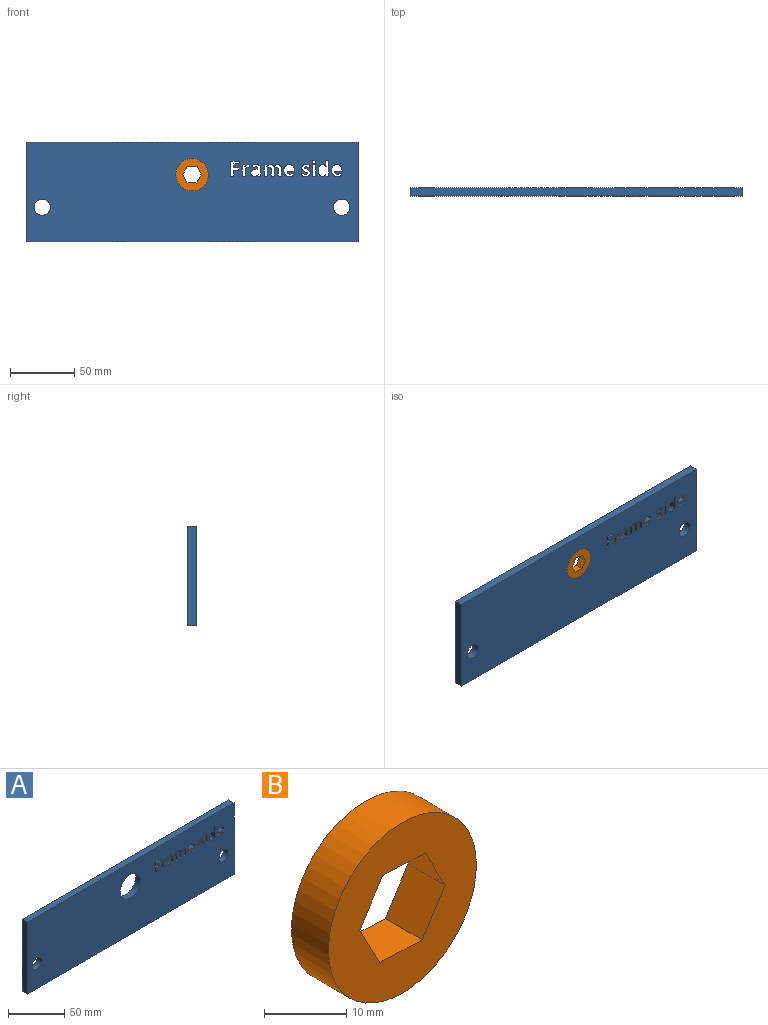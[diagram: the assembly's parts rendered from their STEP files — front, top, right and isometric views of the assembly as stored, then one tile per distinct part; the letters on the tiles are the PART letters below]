
ASSEMBLY  parts=2 mates=1
PART A: 157 faces, bbox 259.1x6.4x77.8 mm
  f0: extruded ~6.35x1.36mm, area 9.2mm2, adj f1,f154,f155,f156
  f1: extruded ~6.35x1.76mm, area 11.3mm2, adj f0,f2,f155,f156
  f2: extruded ~6.35x3.35mm, area 23.2mm2, adj f1,f3,f155,f156
  f3: extruded ~6.35x3.35mm, area 23.3mm2, adj f2,f4,f155,f156
  f4: extruded ~6.35x3.45mm, area 23.6mm2, adj f3,f5,f155,f156
  f5: extruded ~6.35x3.09mm, area 21.7mm2, adj f4,f6,f155,f156
  f6: extruded ~6.35x2.93mm, area 20.4mm2, adj f5,f7,f155,f156
  f7: extruded ~6.35x2.96mm, area 20.5mm2, adj f6,f8,f155,f156
  f8: plane 6.35x1.18mm, normal (-1,0,0), area 7.5mm2, adj f7,f9,f155,f156
  f9: plane 6.35x5.73mm, normal (0,0,1), area 36.4mm2, adj f8,f10,f155,f156
  f10: extruded ~6.35x1.61mm, area 11.2mm2, adj f9,f11,f155,f156
  f11: extruded ~6.35x1.6mm, area 11.1mm2, adj f10,f12,f155,f156
  f12: extruded ~6.35x1.52mm, area 9.7mm2, adj f11,f13,f155,f156
  f13: extruded ~6.35x1.49mm, area 10.1mm2, adj f12,f154,f155,f156
  f14: extruded ~6.35x2.02mm, area 13.3mm2, adj f15,f141,f155,f156
  f15: plane 6.35x4.46mm, normal (-1,0,0), area 28.3mm2, adj f14,f16,f155,f156
  f16: plane 6.35x2.42mm, normal (0,0,1), area 15.4mm2, adj f15,f17,f155,f156
  f17: plane 6.35x5.19mm, normal (1,0,0), area 32.9mm2, adj f16,f18,f155,f156
  f18: extruded ~6.35x1.44mm, area 9.5mm2, adj f17,f19,f155,f156
  f19: extruded ~6.35x1.01mm, area 7.4mm2, adj f18,f20,f155,f156
  f20: extruded ~6.35x1.35mm, area 10.1mm2, adj f19,f21,f155,f156
  f21: extruded ~6.35x2.25mm, area 14.7mm2, adj f20,f22,f155,f156
  f22: plane 6.35x4.18mm, normal (-1,0,0), area 26.5mm2, adj f21,f23,f155,f156
  f23: plane 6.35x2.42mm, normal (0,0,1), area 15.4mm2, adj f22,f24,f155,f156
  f24: plane 8.88x6.35mm, normal (1,0,0), area 56.4mm2, adj f23,f25,f155,f156
  f25: plane 6.35x1.85mm, normal (0,0,-1), area 11.7mm2, adj f24,f26,f155,f156
  f26: plane 6.35x1.14mm, normal (-0.96,0,-0.28), area 7.5mm2, adj f25,f27,f155,f156
  f27: plane 6.35x0.13mm, normal (0,0,-1), area 0.9mm2, adj f26,f28,f155,f156
  f28: extruded ~6.35x1.03mm, area 9.1mm2, adj f27,f29,f155,f156
  f29: extruded ~6.35x1.55mm, area 10.2mm2, adj f28,f30,f155,f156
  f30: extruded ~6.35x2.7mm, area 20.1mm2, adj f29,f31,f155,f156
  f31: plane 6.35x0.21mm, normal (0,0,-1), area 1.4mm2, adj f30,f32,f155,f156
  f32: extruded ~6.35x1.05mm, area 9.2mm2, adj f31,f33,f155,f156
  f33: extruded ~6.35x1.57mm, area 10.3mm2, adj f32,f34,f155,f156
  f34: extruded ~6.35x2.28mm, area 15.7mm2, adj f33,f35,f155,f156
  f35: extruded ~6.35x2.48mm, area 16.9mm2, adj f34,f36,f155,f156
  f36: plane 6.35x5.79mm, normal (-1,0,0), area 36.8mm2, adj f35,f37,f155,f156
  f37: plane 6.35x2.43mm, normal (0,0,1), area 15.4mm2, adj f36,f38,f155,f156
  f38: plane 6.35x5.19mm, normal (1,0,0), area 32.9mm2, adj f37,f39,f155,f156
  f39: extruded ~6.35x1.44mm, area 9.5mm2, adj f38,f40,f155,f156
  f40: extruded ~6.35x1.01mm, area 7.4mm2, adj f39,f141,f155,f156
  f41: plane 6.35x5.92mm, normal (-1,0,0), area 37.6mm2, adj f42,f142,f155,f156
  f42: plane 6.35x1.69mm, normal (0,0,1), area 10.7mm2, adj f41,f43,f155,f156
  f43: plane 6.35x1.21mm, normal (0.93,0,0.36), area 8.2mm2, adj f42,f44,f155,f156
  f44: plane 6.35x0.06mm, normal (0,0,1), area 0.4mm2, adj f43,f45,f155,f156
  f45: extruded ~6.35x1.26mm, area 10.6mm2, adj f44,f46,f155,f156
  f46: extruded ~6.35x1.69mm, area 11mm2, adj f45,f47,f155,f156
  f47: extruded ~6.35x2.01mm, area 14mm2, adj f46,f48,f155,f156
  f48: extruded ~6.35x2.08mm, area 14.4mm2, adj f47,f49,f155,f156
  f49: extruded ~6.35x2.08mm, area 15.3mm2, adj f48,f50,f155,f156
  f50: extruded ~6.35x2.98mm, area 19.8mm2, adj f49,f51,f155,f156
  f51: plane 6.35x1.54mm, normal (0.03,0,-1), area 9.8mm2, adj f50,f52,f155,f156
  f52: plane 6.35x0.39mm, normal (1,0,0), area 2.5mm2, adj f51,f53,f155,f156
  f53: extruded ~6.35x1.38mm, area 14.1mm2, adj f52,f54,f155,f156
  f54: extruded ~6.35x2.5mm, area 16.5mm2, adj f53,f55,f155,f156
  f55: plane 6.35x1.64mm, normal (0.9,0,0.44), area 11.6mm2, adj f54,f56,f155,f156
  f56: extruded ~6.35x3.4mm, area 22.4mm2, adj f55,f57,f155,f156
  f57: extruded ~6.35x2.74mm, area 18.4mm2, adj f56,f142,f155,f156
  f58: extruded ~6.35x1.2mm, area 10.5mm2, adj f59,f143,f155,f156
  f59: extruded ~6.35x1.53mm, area 10.3mm2, adj f58,f60,f155,f156
  f60: extruded ~6.35x0.82mm, area 5.2mm2, adj f59,f61,f155,f156
  f61: plane 6.35x2.27mm, normal (-1,0,0.08), area 14.5mm2, adj f60,f62,f155,f156
  f62: extruded ~6.35x0.71mm, area 4.6mm2, adj f61,f63,f155,f156
  f63: extruded ~6.35x1.81mm, area 12.4mm2, adj f62,f64,f155,f156
  f64: extruded ~6.35x1.67mm, area 11.7mm2, adj f63,f65,f155,f156
  f65: plane 6.35x4.52mm, normal (-1,0,0), area 28.7mm2, adj f64,f66,f155,f156
  f66: plane 6.35x2.42mm, normal (0,0,1), area 15.4mm2, adj f65,f67,f155,f156
  f67: plane 8.88x6.35mm, normal (1,0,0), area 56.4mm2, adj f66,f68,f155,f156
  f68: plane 6.35x1.84mm, normal (0,0,-1), area 11.7mm2, adj f67,f69,f155,f156
  f69: plane 6.35x1.49mm, normal (-0.97,0,-0.23), area 9.8mm2, adj f68,f143,f155,f156
  f70: plane 6.35x3.94mm, normal (0,0,1), area 25mm2, adj f71,f144,f155,f156
  f71: plane 6.35x4.59mm, normal (-1,0,0), area 29.1mm2, adj f70,f72,f155,f156
  f72: plane 6.35x2.42mm, normal (0,0,1), area 15.4mm2, adj f71,f73,f155,f156
  f73: plane 11.61x6.35mm, normal (1,0,0), area 73.7mm2, adj f72,f74,f155,f156
  f74: plane 6.66x6.35mm, normal (0,0,-1), area 42.3mm2, adj f73,f75,f155,f156
  f75: plane 6.35x2.02mm, normal (-1,0,0), area 12.8mm2, adj f74,f76,f155,f156
  f76: plane 6.35x4.23mm, normal (0,0,1), area 26.9mm2, adj f75,f77,f155,f156
  f77: plane 6.35x2.99mm, normal (-1,0,0), area 19mm2, adj f76,f78,f155,f156
  f78: plane 6.35x3.94mm, normal (0,0,-1), area 25mm2, adj f77,f144,f155,f156
  f79: plane 77.8x6.35mm, normal (-1,0,0), area 494mm2, adj f80,f145,f155,f156
  f80: plane 259.08x6.35mm, normal (0,0,-1), area 1645.2mm2, adj f79,f81,f155,f156
  f81: plane 77.8x6.35mm, normal (1,0,0), area 494mm2, adj f80,f145,f155,f156
  f82: extruded ~6.35x1.36mm, area 9.2mm2, adj f83,f146,f155,f156
  f83: extruded ~6.35x1.76mm, area 11.3mm2, adj f82,f84,f155,f156
  f84: extruded ~6.35x3.35mm, area 23.2mm2, adj f83,f85,f155,f156
  f85: extruded ~6.35x3.35mm, area 23.3mm2, adj f84,f86,f155,f156
  f86: extruded ~6.35x3.45mm, area 23.6mm2, adj f85,f87,f155,f156
  f87: extruded ~6.35x3.09mm, area 21.7mm2, adj f86,f88,f155,f156
  f88: extruded ~6.35x2.93mm, area 20.4mm2, adj f87,f89,f155,f156
  f89: extruded ~6.35x2.96mm, area 20.5mm2, adj f88,f90,f155,f156
  f90: plane 6.35x1.18mm, normal (-1,0,0), area 7.5mm2, adj f89,f91,f155,f156
  f91: plane 6.35x5.73mm, normal (0,0,1), area 36.4mm2, adj f90,f92,f155,f156
  f92: extruded ~6.35x1.61mm, area 11.2mm2, adj f91,f93,f155,f156
  f93: extruded ~6.35x1.6mm, area 11.1mm2, adj f92,f94,f155,f156
  f94: extruded ~6.35x1.52mm, area 9.7mm2, adj f93,f95,f155,f156
  f95: extruded ~6.35x1.49mm, area 10.1mm2, adj f94,f146,f155,f156
  f96: extruded ~6.35x0.84mm, area 7.1mm2, adj f97,f147,f155,f156
  f97: extruded ~6.35x1.14mm, area 7.4mm2, adj f96,f98,f155,f156
  f98: extruded ~6.35x2.08mm, area 15.1mm2, adj f97,f99,f155,f156
  f99: extruded ~6.35x2.84mm, area 18.9mm2, adj f98,f100,f155,f156
  f100: extruded ~6.35x1.65mm, area 10.5mm2, adj f99,f101,f155,f156
  f101: extruded ~6.35x1.28mm, area 8.5mm2, adj f100,f102,f155,f156
  f102: plane 6.35x2mm, normal (1,0,0), area 12.7mm2, adj f101,f103,f155,f156
  f103: extruded ~6.35x1.52mm, area 10.2mm2, adj f102,f104,f155,f156
  f104: extruded ~6.35x1.49mm, area 9.6mm2, adj f103,f105,f155,f156
  f105: extruded ~6.35x1.32mm, area 10.9mm2, adj f104,f106,f155,f156
  f106: extruded ~6.35x0.47mm, area 3.2mm2, adj f105,f107,f155,f156
  f107: extruded ~6.35x0.6mm, area 4.6mm2, adj f106,f108,f155,f156
  f108: extruded ~6.35x1.14mm, area 8mm2, adj f107,f109,f155,f156
  f109: extruded ~6.35x1.51mm, area 10.8mm2, adj f108,f110,f155,f156
  f110: extruded ~6.35x0.84mm, area 7mm2, adj f109,f111,f155,f156
  f111: extruded ~6.35x1.16mm, area 7.6mm2, adj f110,f112,f155,f156
  f112: extruded ~6.35x1.83mm, area 13.6mm2, adj f111,f113,f155,f156
  f113: extruded ~6.35x2.6mm, area 17.3mm2, adj f112,f114,f155,f156
  f114: extruded ~6.35x3.12mm, area 20.5mm2, adj f113,f115,f155,f156
  f115: plane 6.35x1.75mm, normal (-0.92,0,0.39), area 12mm2, adj f114,f116,f155,f156
  f116: extruded ~6.35x1.25mm, area 8.5mm2, adj f115,f117,f155,f156
  f117: extruded ~6.35x1.18mm, area 7.6mm2, adj f116,f118,f155,f156
  f118: extruded ~6.35x1.07mm, area 8.7mm2, adj f117,f119,f155,f156
  f119: extruded ~6.35x0.56mm, area 4.4mm2, adj f118,f120,f155,f156
  f120: extruded ~6.35x1.52mm, area 10.6mm2, adj f119,f147,f155,f156
  f121: extruded ~6.35x0.99mm, area 6.8mm2, adj f122,f148,f155,f156
  f122: extruded ~6.35x1.32mm, area 12.9mm2, adj f121,f123,f155,f156
  f123: extruded ~6.35x1.32mm, area 12.9mm2, adj f122,f124,f155,f156
  f124: extruded ~6.35x1.32mm, area 12.9mm2, adj f123,f148,f155,f156
  f125: plane 6.35x2.42mm, normal (0,0,-1), area 15.4mm2, adj f126,f149,f155,f156
  f126: plane 8.88x6.35mm, normal (-1,0,0), area 56.4mm2, adj f125,f127,f155,f156
  f127: plane 6.35x2.42mm, normal (0,0,1), area 15.4mm2, adj f126,f149,f155,f156
  f128: plane 6.35x0.1mm, normal (0,0,1), area 0.7mm2, adj f129,f150,f155,f156
  f129: extruded ~6.35x2.52mm, area 18.9mm2, adj f128,f130,f155,f156
  f130: extruded ~6.35x2.46mm, area 18.1mm2, adj f129,f131,f155,f156
  f131: extruded ~6.35x3.37mm, area 22.5mm2, adj f130,f132,f155,f156
  f132: extruded ~6.35x3.4mm, area 22.7mm2, adj f131,f133,f155,f156
  f133: extruded ~6.35x2.5mm, area 18.4mm2, adj f132,f134,f155,f156
  f134: extruded ~6.35x2.56mm, area 19.1mm2, adj f133,f135,f155,f156
  f135: plane 6.35x0.08mm, normal (0,0,-1), area 0.5mm2, adj f134,f136,f155,f156
  f136: extruded ~6.35x1.77mm, area 11.3mm2, adj f135,f137,f155,f156
  f137: plane 6.35x2.84mm, normal (1,0,0), area 18.1mm2, adj f136,f138,f155,f156
  f138: plane 6.35x2.43mm, normal (0,0,-1), area 15.4mm2, adj f137,f139,f155,f156
  f139: plane 12.36x6.35mm, normal (-1,0,0), area 78.5mm2, adj f138,f140,f155,f156
  f140: plane 6.35x1.86mm, normal (0,0,1), area 11.8mm2, adj f139,f150,f155,f156
  f141: extruded ~6.35x1.33mm, area 9.8mm2, adj f14,f40,f155,f156
  f142: extruded ~6.35x2.37mm, area 16.8mm2, adj f41,f57,f155,f156
  f143: plane 6.35x0.12mm, normal (0,0,-1), area 0.7mm2, adj f58,f69,f155,f156
  f144: plane 6.35x2.01mm, normal (-1,0,0), area 12.8mm2, adj f70,f78,f155,f156
  f145: plane 259.08x6.35mm, normal (0,0,1), area 1645.2mm2, adj f79,f81,f155,f156
  f146: plane 6.35x1.88mm, normal (-1,0,0), area 11.9mm2, adj f82,f95,f155,f156
  f147: extruded ~6.35x1.52mm, area 10.9mm2, adj f96,f120,f155,f156
  f148: extruded ~6.35x0.88mm, area 6.1mm2, adj f121,f124,f155,f156
  f149: plane 8.88x6.35mm, normal (1,0,0), area 56.4mm2, adj f125,f127,f155,f156
  f150: plane 6.35x1.15mm, normal (0.93,0,0.38), area 7.9mm2, adj f128,f140,f155,f156
  f151: cylinder r=6.35mm len=12.7mm, axis (0,1,0), area 253.4mm2, adj f155,f156
  f152: cylinder r=6.35mm len=12.7mm, axis (0,1,0), area 253.4mm2, adj f155,f156
  f153: cylinder r=12.7mm len=25.4mm, axis (0,1,0), area 506.7mm2, adj f155,f156
  f154: plane 6.35x1.88mm, normal (-1,0,0), area 11.9mm2, adj f0,f13,f155,f156
  f155: plane 259.08x77.8mm, normal (0,-1,0), area 18946.4mm2, adj f0,f1,f2,f3,f4,f5,f6,f7
  f156: plane 259.08x77.8mm, normal (0,1,0), area 18946.4mm2, adj f0,f1,f2,f3,f4,f5,f6,f7
PART B: 9 faces, bbox 25.4x6.4x25.4 mm
  f0: plane 7.33x6.35mm, normal (-0.04,0,-1), area 46.6mm2, adj f1,f5,f7,f8
  f1: plane 6.49x6.35mm, normal (-0.89,0,-0.47), area 46.6mm2, adj f0,f2,f7,f8
  f2: plane 6.35x6.2mm, normal (-0.85,0,0.53), area 46.6mm2, adj f1,f3,f7,f8
  f3: plane 7.33x6.35mm, normal (0.04,0,1), area 46.6mm2, adj f2,f4,f7,f8
  f4: plane 6.49x6.35mm, normal (0.89,0,0.47), area 46.6mm2, adj f3,f5,f7,f8
  f5: plane 6.35x6.2mm, normal (0.85,0,-0.53), area 46.6mm2, adj f0,f4,f7,f8
  f6: cylinder r=12.7mm len=25.4mm, axis (0,1,0), area 506.7mm2, adj f7,f8
  f7: plane 25.4x25.4mm, normal (0,-1,0), area 367mm2, adj f0,f1,f2,f3,f4,f5,f6
  f8: plane 25.4x25.4mm, normal (0,1,0), area 367mm2, adj f0,f1,f2,f3,f4,f5,f6
PLACE A t=(-82.62,-32.73,-47.32)mm
PLACE B t=(-140.43,-32.73,43.92)mm
MATE revolute A.f153 <-> B.f6  axis (0,-1,0) through (-47.25,-39.08,5.08)mm
